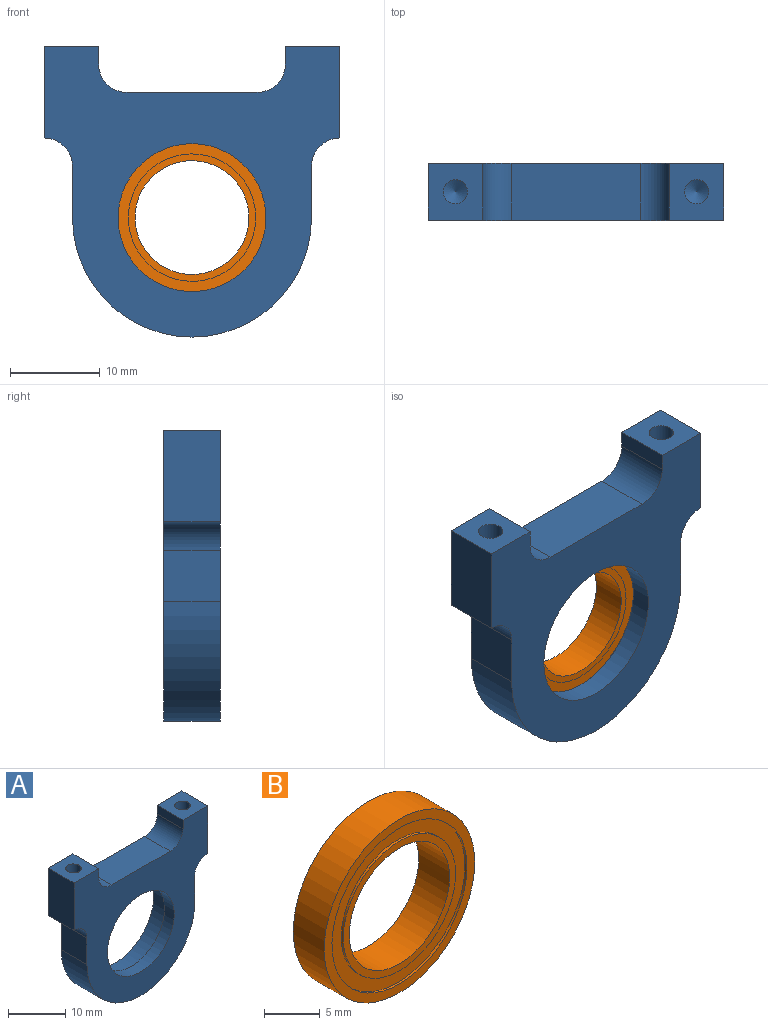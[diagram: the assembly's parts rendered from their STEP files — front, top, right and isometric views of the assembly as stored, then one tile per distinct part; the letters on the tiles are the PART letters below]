
ASSEMBLY  parts=2 mates=1
PART A: 23 faces, bbox 33x6.4x32.4 mm
  f0: cylinder r=8.26mm len=16.51mm, axis (0,1,0), area 123.8mm2, adj f17,f22
  f1: cylinder r=9.53mm len=19.05mm, axis (0,1,0), area 237.1mm2, adj f16,f22
  f2: cylinder r=1.35mm len=7.62mm, axis (0,0,1), area 64.8mm2, adj f3,f9
  f3: cone r=1.35mm half-angle=59deg, axis (0,0,1), area 6.7mm2, adj f2
  f4: cylinder r=1.35mm len=7.62mm, axis (0,0,1), area 64.8mm2, adj f5,f13
  f5: cone r=1.35mm half-angle=59deg, axis (0,0,1), area 6.7mm2, adj f4
  f6: cylinder r=13.33mm len=26.67mm, axis (0,-1,0), area 266mm2, adj f7,f15,f16,f17
  f7: plane 6.35x5.72mm, normal (-1,0,0), area 36.3mm2, adj f6,f16,f17,f18
  f8: plane 10.16x6.35mm, normal (-1,0,0), area 64.5mm2, adj f9,f16,f17,f18
  f9: plane 6.35x6.08mm, normal (0,0,1), area 32.9mm2, adj f2,f8,f10,f16,f17
  f10: plane 6.35x1.91mm, normal (1,0,0), area 12.1mm2, adj f9,f16,f17,f21
  f11: plane 14.51x6.35mm, normal (0,0,1), area 92.1mm2, adj f16,f17,f20,f21
  f12: plane 6.35x1.91mm, normal (-1,0,0), area 12.1mm2, adj f13,f16,f17,f20
  f13: plane 6.35x6.08mm, normal (0,0,1), area 32.9mm2, adj f4,f12,f14,f16,f17
  f14: plane 10.16x6.35mm, normal (1,0,0), area 64.5mm2, adj f13,f16,f17,f19
  f15: plane 6.35x5.72mm, normal (1,0,0), area 36.3mm2, adj f6,f16,f17,f19
  f16: plane 33.02x32.39mm, normal (0,1,0), area 469.6mm2, adj f1,f6,f7,f8,f9,f10,f11,f12
  f17: plane 33.02x32.39mm, normal (0,-1,0), area 540.5mm2, adj f0,f6,f7,f8,f9,f10,f11,f12
  f18: cylinder r=3.17mm len=6.35mm, axis (0,1,0), area 31.7mm2, adj f7,f8,f16,f17
  f19: cylinder r=3.17mm len=6.35mm, axis (0,1,0), area 31.7mm2, adj f14,f15,f16,f17
  f20: cylinder r=3.17mm len=6.35mm, axis (0,1,0), area 31.7mm2, adj f11,f12,f16,f17
  f21: cylinder r=3.17mm len=6.35mm, axis (0,1,0), area 31.7mm2, adj f10,f11,f16,f17
  f22: plane 19.05x19.05mm, normal (0,1,0), area 70.9mm2, adj f0,f1
PART B: 12 faces, bbox 19.1x3.9x19.1 mm
  f0: cylinder r=7.11mm len=14.22mm, axis (0,-1,0), area 11.4mm2, adj f6,f11
  f1: cylinder r=8.55mm len=17.09mm, axis (0,-1,0), area 13.6mm2, adj f9,f11
  f2: cylinder r=7.11mm len=14.22mm, axis (0,1,0), area 11.4mm2, adj f7,f10
  f3: cylinder r=8.55mm len=17.09mm, axis (0,1,0), area 13.6mm2, adj f8,f10
  f4: cylinder r=6.35mm len=12.7mm, axis (0,-1,0), area 156.1mm2, adj f6,f7
  f5: cylinder r=9.53mm len=19.05mm, axis (0,-1,0), area 234.1mm2, adj f8,f9
  f6: plane 14.22x14.22mm, normal (0,-1,0), area 32.2mm2, adj f0,f4
  f7: plane 14.22x14.22mm, normal (0,1,0), area 32.2mm2, adj f2,f4
  f8: plane 19.05x19.05mm, normal (0,1,0), area 55.5mm2, adj f3,f5
  f9: plane 19.05x19.05mm, normal (0,-1,0), area 55.5mm2, adj f1,f5
  f10: plane 17.09x17.09mm, normal (0,1,0), area 70.6mm2, adj f2,f3
  f11: plane 17.09x17.09mm, normal (0,-1,0), area 70.6mm2, adj f0,f1
PLACE A t=(9.98,13.11,24.37)mm
PLACE B rot(axis=(0,-1,0),90deg) t=(9.98,15.5,24.37)mm
MATE fastened B.f0 <-> A.f0  axis (0,1,0) through (9.98,15.5,24.37)mm
